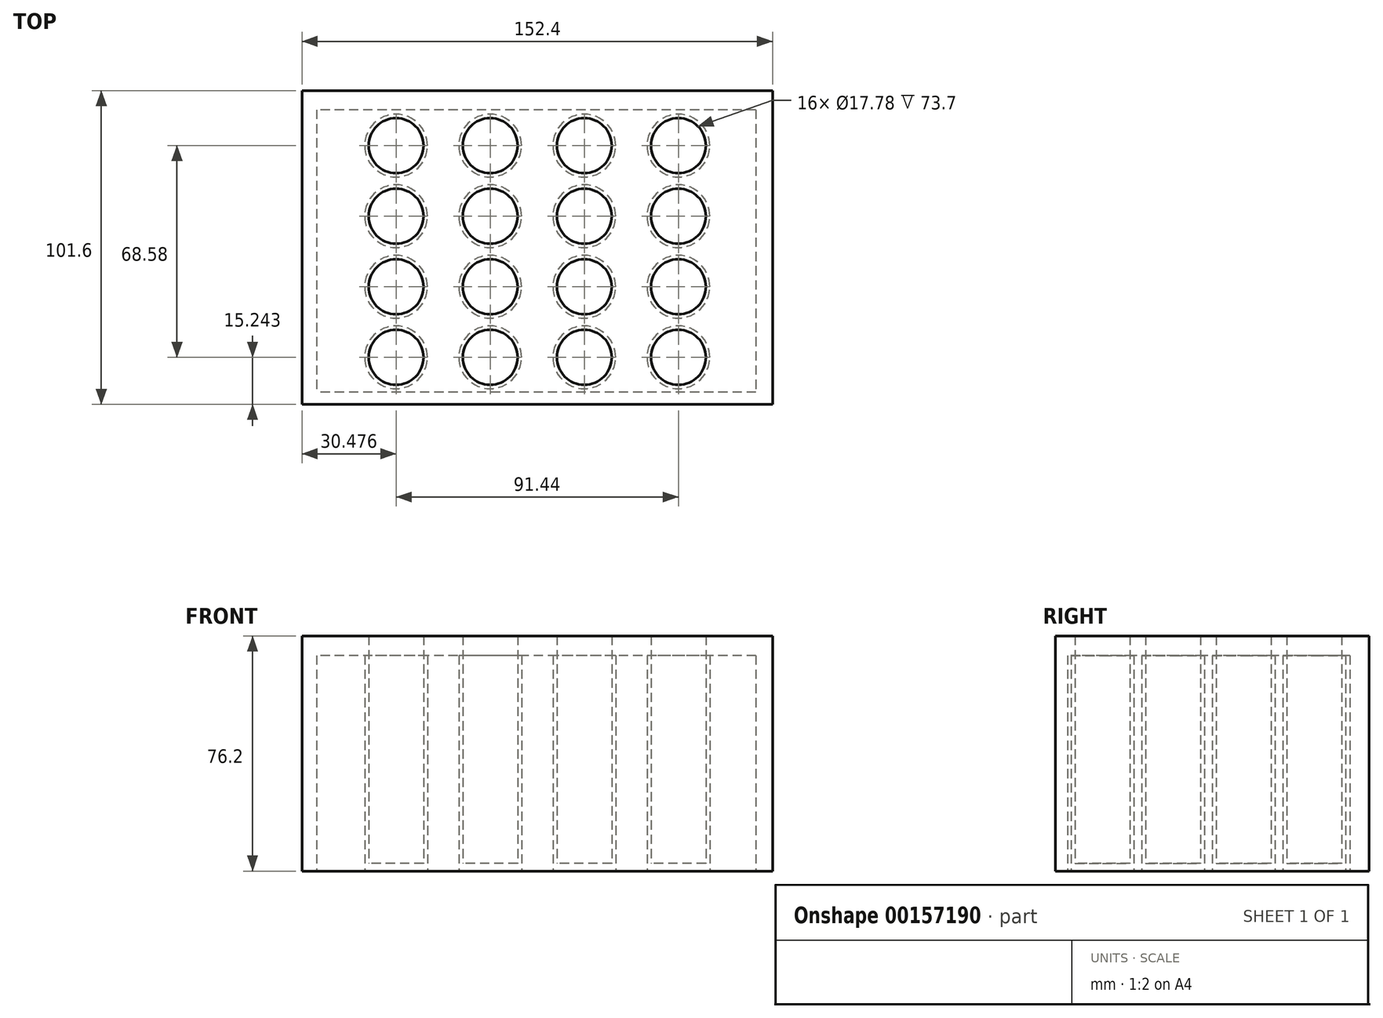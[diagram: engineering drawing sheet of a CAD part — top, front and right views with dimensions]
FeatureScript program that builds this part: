
annotation { "Feature Type Name" : "Feature", "Feature Type Description" : "" }
export const myFeature = defineFeature(function(context is Context, id is Id, definition is map)
    precondition{}
    {
        {
            var Q0;
            Q0=qCreatedBy(makeId("Top.planeOp"),FACE);
            var sketch = newSketch(context, id + "F0", { "sketchPlane" : qUnion([Q0])});
            skLineSegment(sketch, "E0.bottom", {"start": v(-75.93, 51.92) * mm, "end": v(76.47, 51.92) * mm});
            skLineSegment(sketch, "E0.top", {"start": v(-75.93, -49.68) * mm, "end": v(76.47, -49.68) * mm});
            skLineSegment(sketch, "E0.left", {"start": v(-75.93, 51.92) * mm, "end": v(-75.93, -49.68) * mm});
            skLineSegment(sketch, "E0.right", {"start": v(76.47, 51.92) * mm, "end": v(76.47, -49.68) * mm});
            skCircle(sketch, "E1", {"center": v(-45.45, 34.14) * mm, "radius": 8.9 * mm});
            skCircle(sketch, "E2", {"center": v(-14.97, 11.28) * mm, "radius": 8.9 * mm});
            skCircle(sketch, "E3", {"center": v(15.5, 34.14) * mm, "radius": 8.9 * mm});
            skCircle(sketch, "E4", {"center": v(45.99, 34.14) * mm, "radius": 8.9 * mm});
            skCircle(sketch, "E5", {"center": v(15.5, 11.28) * mm, "radius": 8.9 * mm});
            skCircle(sketch, "E6", {"center": v(45.99, 11.28) * mm, "radius": 8.9 * mm});
            skCircle(sketch, "E7", {"center": v(-14.97, 34.14) * mm, "radius": 8.9 * mm});
            skCircle(sketch, "E8", {"center": v(-45.45, 11.28) * mm, "radius": 8.9 * mm});
            skCircle(sketch, "E9", {"center": v(-45.45, -11.58) * mm, "radius": 8.9 * mm});
            skCircle(sketch, "E10", {"center": v(-45.45, -34.44) * mm, "radius": 8.9 * mm});
            skCircle(sketch, "E11", {"center": v(-14.97, -34.44) * mm, "radius": 8.9 * mm});
            skCircle(sketch, "E12", {"center": v(15.5, -11.58) * mm, "radius": 8.9 * mm});
            skCircle(sketch, "E13", {"center": v(45.99, -11.58) * mm, "radius": 8.9 * mm});
            skCircle(sketch, "E14", {"center": v(15.5, -34.44) * mm, "radius": 8.9 * mm});
            skCircle(sketch, "E15", {"center": v(45.99, -34.44) * mm, "radius": 8.9 * mm});
            skLineSegment(sketch, "E16", {"start": v(-45.45, 51.92) * mm, "end": v(-45.45, -49.68) * mm, "construction": true});
            skLineSegment(sketch, "E17", {"start": v(-14.97, 51.92) * mm, "end": v(-14.97, -49.68) * mm, "construction": true});
            skLineSegment(sketch, "E18", {"start": v(15.5, 51.92) * mm, "end": v(15.5, -49.68) * mm, "construction": true});
            skLineSegment(sketch, "E19", {"start": v(45.99, 51.92) * mm, "end": v(45.99, -49.68) * mm, "construction": true});
            skLineSegment(sketch, "E20", {"start": v(-75.93, 34.14) * mm, "end": v(76.47, 34.14) * mm, "construction": true});
            skLineSegment(sketch, "E21", {"start": v(-75.93, 11.28) * mm, "end": v(76.47, 11.28) * mm, "construction": true});
            skLineSegment(sketch, "E22", {"start": v(-75.93, -11.58) * mm, "end": v(76.47, -11.58) * mm, "construction": true});
            skLineSegment(sketch, "E23", {"start": v(-76, -34.44) * mm, "end": v(76, -34.44) * mm, "construction": true});
            skCircle(sketch, "E24", {"center": v(-14.97, -11.58) * mm, "radius": 8.9 * mm});
            skSolve(sketch);
        }
        {
            var Q0;
            Q0 = qSketchRegion(id + "F0", true);
            var Q1;
            Q1=makeQuery(id+"F0.imprint","IMPRINT",FACE,{"disambiguationData":[TD([[makeQuery(id+"F0.imprint","IMPRINT",EDGE,{"derivedFrom":sQuery(id+"F0.wireOp",EDGE,"E10")}),1.0]])]});
            var Q2;
            Q2=makeQuery(id+"F0.imprint","IMPRINT",FACE,{"disambiguationData":[TD([[makeQuery(id+"F0.imprint","IMPRINT",EDGE,{"derivedFrom":sQuery(id+"F0.wireOp",EDGE,"E11")}),1.0]])]});
            var Q3;
            Q3=makeQuery(id+"F0.imprint","IMPRINT",FACE,{"disambiguationData":[TD([[makeQuery(id+"F0.imprint","IMPRINT",EDGE,{"derivedFrom":sQuery(id+"F0.wireOp",EDGE,"E24")}),1.0]])]});
            var Q4;
            Q4=makeQuery(id+"F0.imprint","IMPRINT",FACE,{"disambiguationData":[TD([[makeQuery(id+"F0.imprint","IMPRINT",EDGE,{"derivedFrom":sQuery(id+"F0.wireOp",EDGE,"E9")}),1.0]])]});
            var Q5;
            Q5=makeQuery(id+"F0.imprint","IMPRINT",FACE,{"disambiguationData":[TD([[makeQuery(id+"F0.imprint","IMPRINT",EDGE,{"derivedFrom":sQuery(id+"F0.wireOp",EDGE,"E8")}),1.0]])]});
            var Q6;
            Q6=makeQuery(id+"F0.imprint","IMPRINT",FACE,{"disambiguationData":[TD([[makeQuery(id+"F0.imprint","IMPRINT",EDGE,{"derivedFrom":sQuery(id+"F0.wireOp",EDGE,"E1")}),1.0]])]});
            var Q7;
            Q7=makeQuery(id+"F0.imprint","IMPRINT",FACE,{"disambiguationData":[TD([[makeQuery(id+"F0.imprint","IMPRINT",EDGE,{"derivedFrom":sQuery(id+"F0.wireOp",EDGE,"E7")}),1.0]])]});
            var Q8;
            Q8=makeQuery(id+"F0.imprint","IMPRINT",FACE,{"disambiguationData":[TD([[makeQuery(id+"F0.imprint","IMPRINT",EDGE,{"derivedFrom":sQuery(id+"F0.wireOp",EDGE,"E2")}),1.0]])]});
            var Q9;
            Q9=makeQuery(id+"F0.imprint","IMPRINT",FACE,{"disambiguationData":[TD([[makeQuery(id+"F0.imprint","IMPRINT",EDGE,{"derivedFrom":sQuery(id+"F0.wireOp",EDGE,"E3")}),1.0]])]});
            var Q10;
            Q10=makeQuery(id+"F0.imprint","IMPRINT",FACE,{"disambiguationData":[TD([[makeQuery(id+"F0.imprint","IMPRINT",EDGE,{"derivedFrom":sQuery(id+"F0.wireOp",EDGE,"E5")}),1.0]])]});
            var Q11;
            Q11=makeQuery(id+"F0.imprint","IMPRINT",FACE,{"disambiguationData":[TD([[makeQuery(id+"F0.imprint","IMPRINT",EDGE,{"derivedFrom":sQuery(id+"F0.wireOp",EDGE,"E12")}),1.0]])]});
            var Q12;
            Q12=makeQuery(id+"F0.imprint","IMPRINT",FACE,{"disambiguationData":[TD([[makeQuery(id+"F0.imprint","IMPRINT",EDGE,{"derivedFrom":sQuery(id+"F0.wireOp",EDGE,"E14")}),1.0]])]});
            var Q13;
            Q13=makeQuery(id+"F0.imprint","IMPRINT",FACE,{"disambiguationData":[TD([[makeQuery(id+"F0.imprint","IMPRINT",EDGE,{"derivedFrom":sQuery(id+"F0.wireOp",EDGE,"E15")}),1.0]])]});
            var Q14;
            Q14=makeQuery(id+"F0.imprint","IMPRINT",FACE,{"disambiguationData":[TD([[makeQuery(id+"F0.imprint","IMPRINT",EDGE,{"derivedFrom":sQuery(id+"F0.wireOp",EDGE,"E13")}),1.0]])]});
            var Q15;
            Q15=makeQuery(id+"F0.imprint","IMPRINT",FACE,{"disambiguationData":[TD([[makeQuery(id+"F0.imprint","IMPRINT",EDGE,{"derivedFrom":sQuery(id+"F0.wireOp",EDGE,"E6")}),1.0]])]});
            var Q16;
            Q16=makeQuery(id+"F0.imprint","IMPRINT",FACE,{"disambiguationData":[TD([[makeQuery(id+"F0.imprint","IMPRINT",EDGE,{"derivedFrom":sQuery(id+"F0.wireOp",EDGE,"E4")}),1.0]])]});
            extrude(context, id + "F1", {"entities" : qUnion([Q0, Q1, Q2, Q3, Q4, Q5, Q6, Q7, Q8, Q9, Q10, Q11, Q12, Q13, Q14, Q15, Q16]), "depth" : 2.5 * mm});
        }
        {
            var Q0;
            Q0=makeQuery(id+"F0.imprint","IMPRINT",FACE,{"disambiguationData":[TD([[makeQuery(id+"F0.imprint","IMPRINT",EDGE,{"derivedFrom":sQuery(id+"F0.wireOp",EDGE,"E0.bottom")}),-1.0]])]});
            extrude(context, id + "F2", {"entities" : qUnion([Q0]), "operationType" : NewBodyOperationType.ADD, "depth" : 76.2 * mm});
        }
        {
            var Q0;
            Q0=makeQuery(id+"F2.opExtrude","CAP_FACE",FACE,{"disambiguationData":[OSD([sQuery(id+"F0.wireOp",EDGE,"E0.bottom"),sQuery(id+"F0.wireOp",EDGE,"E0.top"),sQuery(id+"F0.wireOp",EDGE,"E0.left"),sQuery(id+"F0.wireOp",EDGE,"E0.right"),sQuery(id+"F0.wireOp",EDGE,"E1"),sQuery(id+"F0.wireOp",EDGE,"E2"),sQuery(id+"F0.wireOp",EDGE,"E3"),sQuery(id+"F0.wireOp",EDGE,"E4"),sQuery(id+"F0.wireOp",EDGE,"E5"),sQuery(id+"F0.wireOp",EDGE,"E6"),sQuery(id+"F0.wireOp",EDGE,"E7"),sQuery(id+"F0.wireOp",EDGE,"E8"),sQuery(id+"F0.wireOp",EDGE,"E9"),sQuery(id+"F0.wireOp",EDGE,"E10"),sQuery(id+"F0.wireOp",EDGE,"E11"),sQuery(id+"F0.wireOp",EDGE,"E12"),sQuery(id+"F0.wireOp",EDGE,"E13"),sQuery(id+"F0.wireOp",EDGE,"E14"),sQuery(id+"F0.wireOp",EDGE,"E15"),sQuery(id+"F0.wireOp",EDGE,"E24")])],"isStart":false});
            var sketch = newSketch(context, id + "F3", { "sketchPlane" : qUnion([Q0])});
            skCircle(sketch, "E25.0", {"center": v(-45.45, 34.14) * mm, "radius": 8.9 * mm});
            skCircle(sketch, "E26", {"center": v(-45.45, 34.14) * mm, "radius": 10.16 * mm});
            skCircle(sketch, "E27.0.1.0", {"center": v(-45.45, 11.28) * mm, "radius": 10.16 * mm});
            skCircle(sketch, "E27.0.2.0", {"center": v(-45.45, -11.58) * mm, "radius": 10.16 * mm});
            skCircle(sketch, "E27.0.3.0", {"center": v(-45.45, -34.44) * mm, "radius": 10.16 * mm});
            skCircle(sketch, "E27.1.0.0", {"center": v(-14.97, 34.14) * mm, "radius": 10.16 * mm});
            skCircle(sketch, "E27.1.1.0", {"center": v(-14.97, 11.28) * mm, "radius": 10.16 * mm});
            skCircle(sketch, "E27.1.2.0", {"center": v(-14.97, -11.58) * mm, "radius": 10.16 * mm});
            skCircle(sketch, "E27.1.3.0", {"center": v(-14.97, -34.44) * mm, "radius": 10.16 * mm});
            skCircle(sketch, "E27.2.0.0", {"center": v(15.5, 34.14) * mm, "radius": 10.16 * mm});
            skCircle(sketch, "E27.2.1.0", {"center": v(15.5, 11.28) * mm, "radius": 10.16 * mm});
            skCircle(sketch, "E27.2.2.0", {"center": v(15.5, -11.58) * mm, "radius": 10.16 * mm});
            skCircle(sketch, "E27.2.3.0", {"center": v(15.5, -34.44) * mm, "radius": 10.16 * mm});
            skCircle(sketch, "E27.3.0.0", {"center": v(45.99, 34.14) * mm, "radius": 10.16 * mm});
            skCircle(sketch, "E27.3.1.0", {"center": v(45.99, 11.28) * mm, "radius": 10.16 * mm});
            skCircle(sketch, "E27.3.2.0", {"center": v(45.99, -11.58) * mm, "radius": 10.16 * mm});
            skCircle(sketch, "E27.3.3.0", {"center": v(45.99, -34.44) * mm, "radius": 10.16 * mm});
            skLineSegment(sketch, "E27.direction1", {"start": v(-45.45, 34.14) * mm, "end": v(-14.97, 34.14) * mm, "construction": true});
            skLineSegment(sketch, "E27.direction2", {"start": v(-45.45, 34.14) * mm, "end": v(-45.45, 11.28) * mm, "construction": true});
            skLineSegment(sketch, "E28.bottom", {"start": v(71.12, 45.72) * mm, "end": v(-71.12, 45.72) * mm});
            skLineSegment(sketch, "E28.top", {"start": v(71.12, -45.72) * mm, "end": v(-71.12, -45.72) * mm});
            skLineSegment(sketch, "E28.left", {"start": v(71.12, 45.72) * mm, "end": v(71.12, -45.72) * mm});
            skLineSegment(sketch, "E28.right", {"start": v(-71.12, 45.72) * mm, "end": v(-71.12, -45.72) * mm});
            skPoint(sketch, "E28.middle", {"position": v(0, 0) * mm});
            skSolve(sketch);
        }
        {
            var Q0;
            Q0=makeQuery(id+"F0.imprint","IMPRINT",FACE,{"disambiguationData":[TD([[makeQuery(id+"F0.imprint","IMPRINT",EDGE,{"derivedFrom":sQuery(id+"F0.wireOp",EDGE,"E0.bottom")}),-1.0]])]});
            var sketch = newSketch(context, id + "F4", { "sketchPlane" : qUnion([Q0])});
            skLineSegment(sketch, "E29.0", {"start": v(71.12, 45.72) * mm, "end": v(-71.12, 45.72) * mm});
            skLineSegment(sketch, "E30.0", {"start": v(-71.12, 45.72) * mm, "end": v(-71.12, -45.72) * mm});
            skLineSegment(sketch, "E31.0", {"start": v(71.12, -45.72) * mm, "end": v(-71.12, -45.72) * mm});
            skLineSegment(sketch, "E32.0", {"start": v(71.12, 45.72) * mm, "end": v(71.12, -45.72) * mm});
            skLineSegment(sketch, "E33.0", {"start": v(-45.45, 34.14) * mm, "end": v(-14.97, 34.14) * mm});
            skCircle(sketch, "E34.0", {"center": v(-45.45, 34.14) * mm, "radius": 10.16 * mm});
            skCircle(sketch, "E35.0", {"center": v(-14.97, 34.14) * mm, "radius": 10.16 * mm});
            skCircle(sketch, "E36.0", {"center": v(15.5, 34.14) * mm, "radius": 10.16 * mm});
            skCircle(sketch, "E37.0", {"center": v(45.99, 34.14) * mm, "radius": 10.16 * mm});
            skCircle(sketch, "E38.0", {"center": v(45.99, 11.28) * mm, "radius": 10.16 * mm});
            skCircle(sketch, "E39.0", {"center": v(15.5, 11.28) * mm, "radius": 10.16 * mm});
            skCircle(sketch, "E40.0", {"center": v(-14.97, 11.28) * mm, "radius": 10.16 * mm});
            skCircle(sketch, "E41.0", {"center": v(-45.45, 11.28) * mm, "radius": 10.16 * mm});
            skCircle(sketch, "E42.0", {"center": v(-45.45, -11.58) * mm, "radius": 10.16 * mm});
            skCircle(sketch, "E43.0", {"center": v(-14.97, -11.58) * mm, "radius": 10.16 * mm});
            skCircle(sketch, "E44.0", {"center": v(15.5, -11.58) * mm, "radius": 10.16 * mm});
            skCircle(sketch, "E45.0", {"center": v(45.99, -11.58) * mm, "radius": 10.16 * mm});
            skCircle(sketch, "E46.0", {"center": v(45.99, -34.44) * mm, "radius": 10.16 * mm});
            skCircle(sketch, "E47.0", {"center": v(15.5, -34.44) * mm, "radius": 10.16 * mm});
            skCircle(sketch, "E48.0", {"center": v(-14.97, -34.44) * mm, "radius": 10.16 * mm});
            skCircle(sketch, "E49.0", {"center": v(-45.45, -34.44) * mm, "radius": 10.16 * mm});
            skSolve(sketch);
        }
        {
            var Q0;
            Q0 = qSketchRegion(id + "F4", true);
            extrude(context, id + "F5", {"entities" : qUnion([Q0]), "operationType" : NewBodyOperationType.REMOVE, "depth" : 69.85 * mm});
        }
    });
